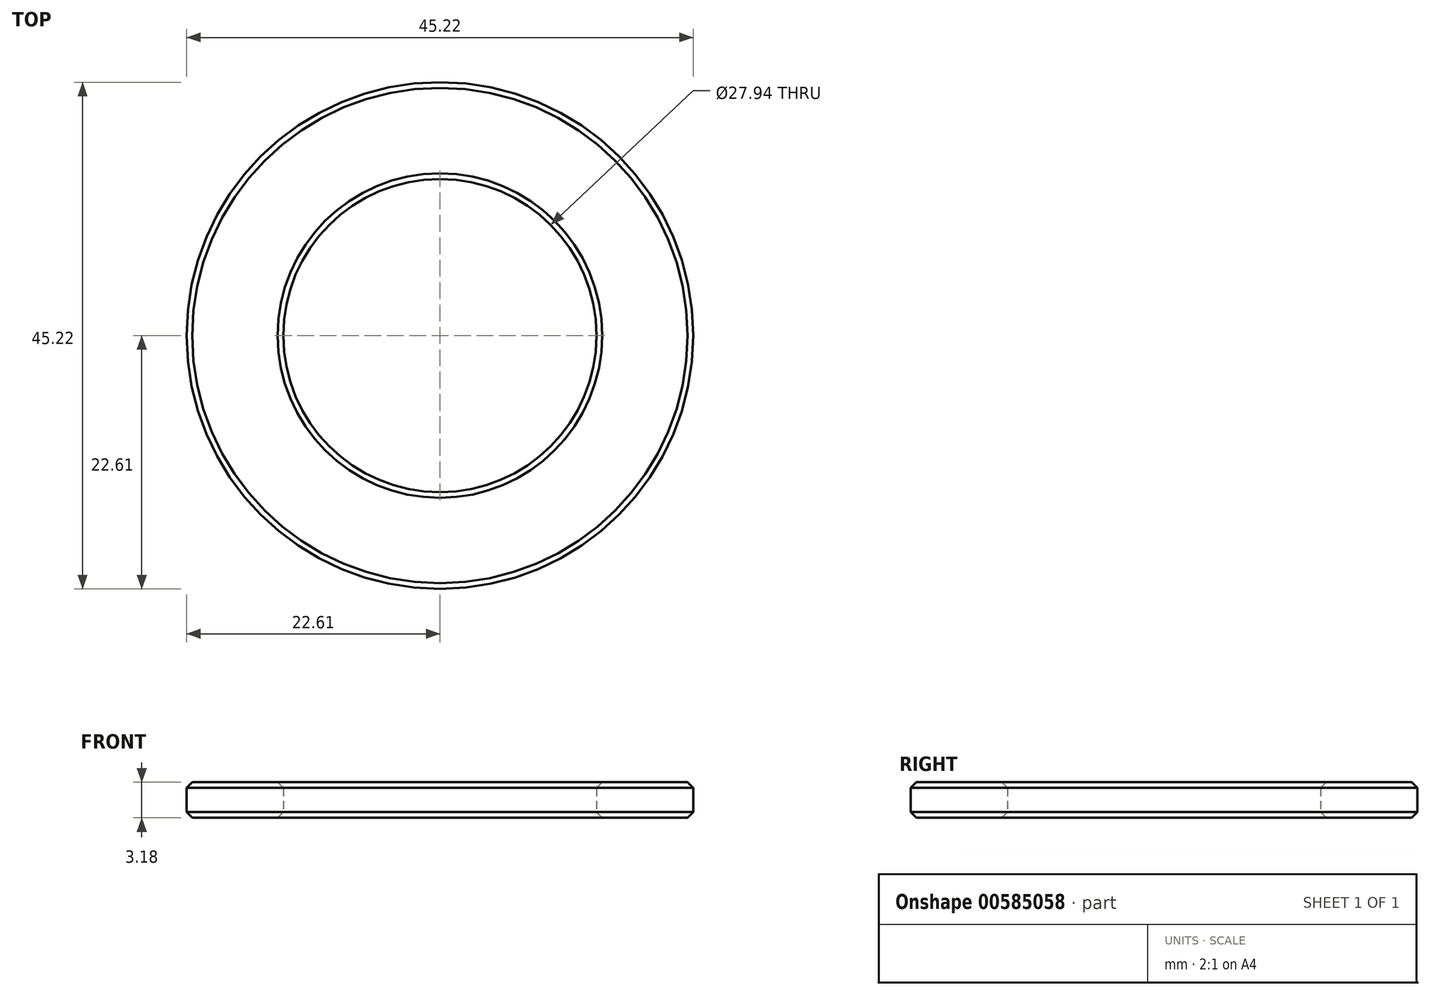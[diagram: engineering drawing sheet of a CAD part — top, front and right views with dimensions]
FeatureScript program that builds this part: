
annotation { "Feature Type Name" : "Feature", "Feature Type Description" : "" }
export const myFeature = defineFeature(function(context is Context, id is Id, definition is map)
    precondition{}
    {
        {
            var Q0;
            Q0=qCreatedBy(makeId("Top.planeOp"),FACE);
            var sketch = newSketch(context, id + "F0", { "sketchPlane" : qUnion([Q0])});
            skCircle(sketch, "E0", {"center": v(0, 0) * mm, "radius": 22.6 * mm});
            skCircle(sketch, "E1", {"center": v(0, 0) * mm, "radius": 13.97 * mm});
            skSolve(sketch);
        }
        {
            var Q0;
            Q0 = qSketchRegion(id + "F0", true);
            extrude(context, id + "F1", {"entities" : qUnion([Q0]), "depth" : 3.17 * mm, "offsetDistance" : 25.4 * mm});
        }
        {
            var Q0;
            Q0=makeQuery(id+"F1.opExtrude","CAP_EDGE",EDGE,{"disambiguationData":[OSD([sQuery(id+"F0.wireOp",EDGE,"E0")])],"isStart":false});
            var Q1;
            Q1=makeQuery(id+"F1.opExtrude","CAP_EDGE",EDGE,{"disambiguationData":[OSD([sQuery(id+"F0.wireOp",EDGE,"E0")])],"isStart":true});
            var Q2;
            Q2=makeQuery(id+"F1.opExtrude","CAP_EDGE",EDGE,{"disambiguationData":[OSD([sQuery(id+"F0.wireOp",EDGE,"E1")])],"isStart":false});
            var Q3;
            Q3=makeQuery(id+"F1.opExtrude","CAP_EDGE",EDGE,{"disambiguationData":[OSD([sQuery(id+"F0.wireOp",EDGE,"E1")])],"isStart":true});
            chamfer(context, id + "F2", {"entities" : qUnion([Q0, Q1, Q2, Q3]), "width" : 0.5 * mm, "tangentPropagation" : true});
        }
    });
